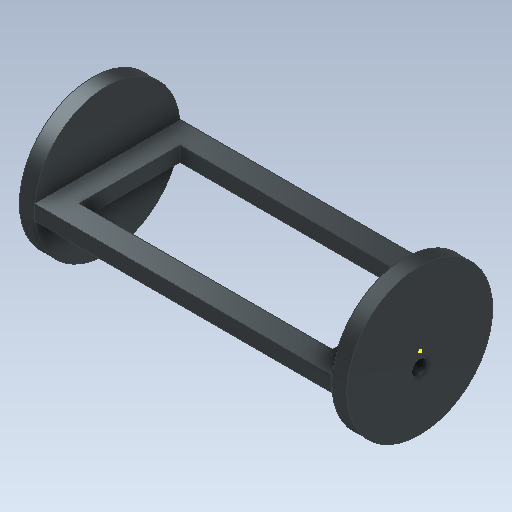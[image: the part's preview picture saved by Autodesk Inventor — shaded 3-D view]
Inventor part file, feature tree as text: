
AUTODESK INVENTOR PART (.ipt)
format: ipt  version: 2020.3 (Build 243373000, 373)  size: 151,552 bytes
history: native  units: mm
features: sketch x4, extrude x3, revolve x1
ambient origin geometry x8: Origin, YZ Plane, XZ Plane, XY Plane, X Axis, Y Axis, Z Axis, Center Point
bodies: Solid1 (feature_tree)
feature tree (8):
  sketch  "Sketch1"  dims[d0=24.5mm d1=5.0mm]
  sketch  "Sketch2"  dims[d2=22.0mm d3=100.0mm]
  revolve  "Revolution1"  [1 undecoded]
  extrude  "Extrusion1"  Depth=100.0mm
  extrude  "Extrusion2"  TaperAngle=90.0deg  [1 undecoded]
  extrude  "Extrusion3"  Depth=49.0mm TaperAngle=0.0deg
  sketch  "Sketch3"  dims[d4=5.0mm d5=90.0deg]
  sketch  "Sketch4"  dims[d6=5.0mm d7=49.0mm d8=0.0mm d9=7.5mm d10=20.0mm d11=0.0mm d13=5.0mm d14=10.0mm d15=0.0mm d16=5.0mm]
note: 2 required parameter values undecoded (feature->parameter linkage not recoverable at this tier; creation-order binding heuristic only, values carry confidence <= 0.55)